# Revit family: QCF-125CO
name_source: partatom
category: Mechanical Equipment
revit_build: Autodesk Revit 2016 (Build: 20150220_1215(x64)
units: mm (PartAtom-declared; Revit-internal decimal feet)

## family parameters
Always vertical = Yes
Cut with Voids When Loaded = No
OmniClass Number = 23.75.70.21.24.11
OmniClass Title = Constant Volume Air Terminal Units
Part Type = Normal
Room Calculation Point = No
Round Connector Dimension = Use Diameter
Shared = No
Work Plane-Based = Yes

## types (2) — shared parameters
Default Elevation = 72 "
Description = Bathroom Fan
Manufacturer = REVERSOMATIC
Model = QCF-110ES
URL = http://www.reversomatic.com

## per-type parameters (varying)
| type | CFM |
| QCF-125CO Low Speed | SP 0/CFM 88 - SP 0.05/CFM 79 - SP 0.10/CFM 72 - SP 0.15/CFM 68 - SP 0.20/CFM 62 - SP 0.25/CFM 45 - SP 0.30/CFM 40 |
| QCF-125CO High Speed | SP 0/CFM 126 - SP 0.05/CFM 120 - SP 0.10/CFM 118 - SP 0.15/CFM 116 - SP 0.20/CFM 115 - SP 0.25/CFM 112 - SP 0.30/CFM 108 - SP 0.40/CFM 90 - SP 0.50/CFM 66 |

## geometry (parser evidence)
native form markers: Sweep x2
no freeform markers — native parametric forms only
